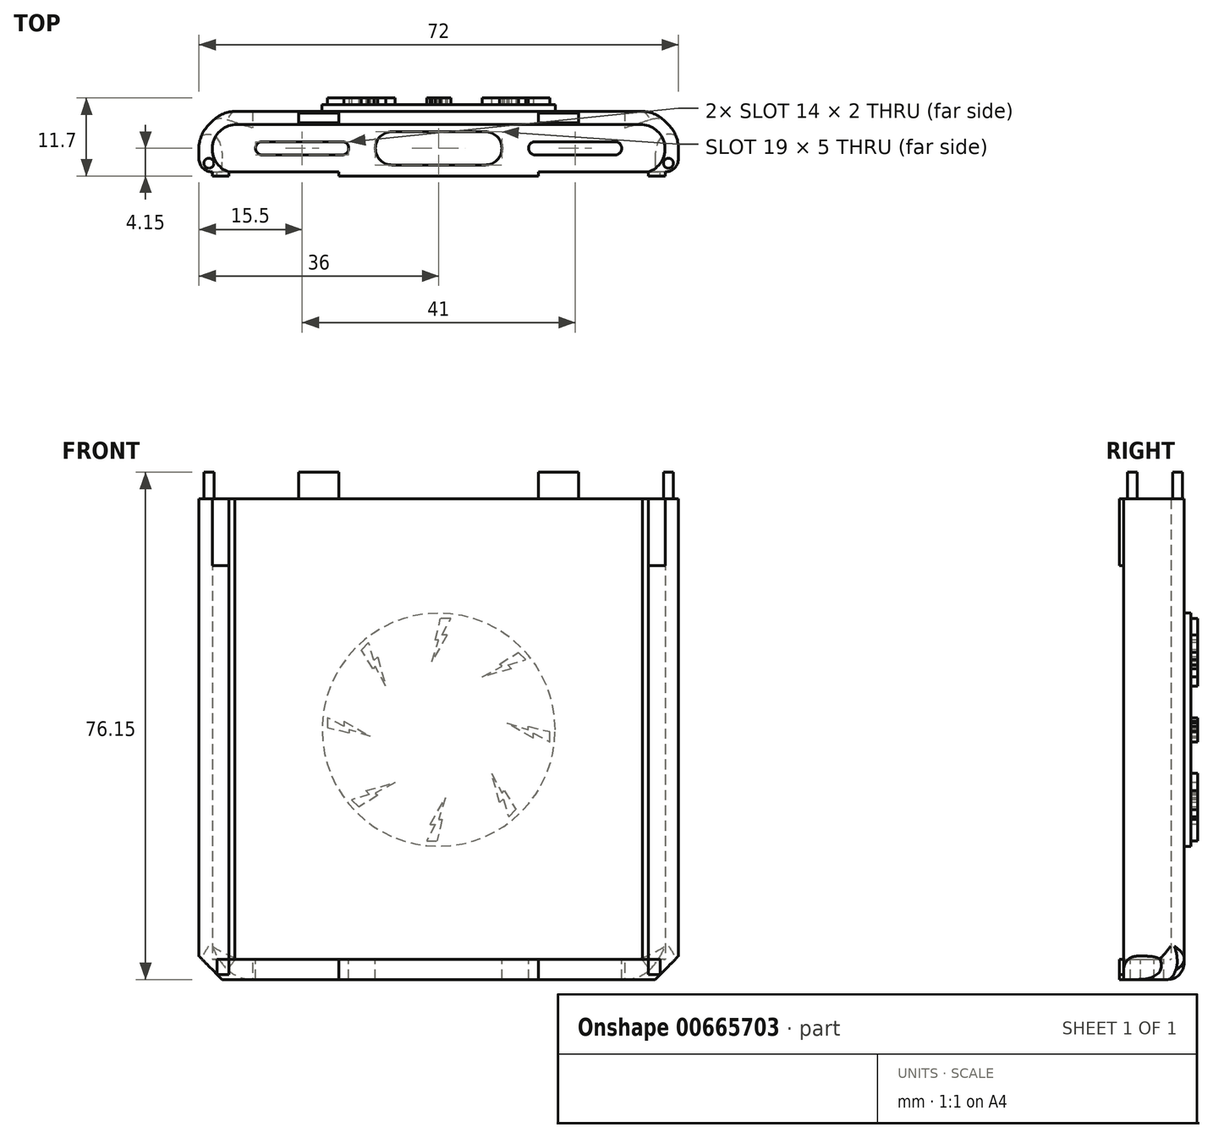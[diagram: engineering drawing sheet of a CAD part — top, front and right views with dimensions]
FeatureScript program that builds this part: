
annotation { "Feature Type Name" : "Feature", "Feature Type Description" : "" }
export const myFeature = defineFeature(function(context is Context, id is Id, definition is map)
    precondition{}
    {
        {
            var Q0;
            Q0=qCreatedBy(makeId("Top.planeOp"),FACE);
            var sketch = newSketch(context, id + "F0", { "sketchPlane" : qUnion([Q0])});
            skLineSegment(sketch, "E0.bottom", {"start": v(-36, 4.55) * mm, "end": v(36, 4.55) * mm});
            skLineSegment(sketch, "E0.top", {"start": v(-36, -4.55) * mm, "end": v(36, -4.55) * mm});
            skLineSegment(sketch, "E0.left", {"start": v(-36, 4.55) * mm, "end": v(-36, -4.55) * mm});
            skLineSegment(sketch, "E0.right", {"start": v(36, 4.55) * mm, "end": v(36, -4.55) * mm});
            skPoint(sketch, "E0.middle", {"position": v(0, 0) * mm});
            skLineSegment(sketch, "E1.bottom", {"start": v(34, -4.55) * mm, "end": v(-34, -4.55) * mm});
            skLineSegment(sketch, "E1.top", {"start": v(34, 2.55) * mm, "end": v(-34, 2.55) * mm});
            skLineSegment(sketch, "E1.left", {"start": v(34, -4.55) * mm, "end": v(34, 2.55) * mm});
            skLineSegment(sketch, "E1.right", {"start": v(-34, -4.55) * mm, "end": v(-34, 2.55) * mm});
            skArc(sketch, "E2", {"start": v(-30.6, 2.55) * mm, "mid": v(-33.97, -0.63) * mm, "end": v(-31.5, -4.55) * mm});
            skArc(sketch, "E3", {"start": v(31.5, -4.55) * mm, "mid": v(33.97, -0.63) * mm, "end": v(30.6, 2.55) * mm});
            skSolve(sketch);
        }
        {
            var Q0;
            Q0=makeQuery(id+"F0.imprint","IMPRINT",FACE,{"disambiguationData":[TD([[makeQuery(id+"F0.imprint","IMPRINT",EDGE,{"derivedFrom":sQuery(id+"F0.wireOp",EDGE,"E0.bottom")}),-1.0]])]});
            var Q1;
            {var subQ0=sQuery(id+"F0.wireOp",EDGE,"E3");var subQ1=sQuery(id+"F0.wireOp",EDGE,"E1.top");var subQ2=makeQuery(id+"F0.imprint","INTERSECT",VERTEX,{"derivedFrom":[subQ1,subQ0]});Q1=makeQuery(id+"F0.imprint","IMPRINT",FACE,{"disambiguationData":[TD([[makeQuery(id+"F0.imprint","IMPRINT",EDGE,{"disambiguationData":[TD([[subQ2,1.0]])],"derivedFrom":subQ1}),1.0]])]});}
            var Q2;
            {var subQ0=sQuery(id+"F0.wireOp",EDGE,"E3");var subQ1=sQuery(id+"F0.wireOp",EDGE,"E0.top");var subQ2=makeQuery(id+"F0.imprint","INTERSECT",VERTEX,{"derivedFrom":[subQ1,subQ0]});Q2=makeQuery(id+"F0.imprint","IMPRINT",FACE,{"disambiguationData":[TD([[makeQuery(id+"F0.imprint","IMPRINT",EDGE,{"disambiguationData":[TD([[subQ2,-1.0]])],"derivedFrom":subQ1}),1.0]])]});}
            var Q3;
            {var subQ0=sQuery(id+"F0.wireOp",EDGE,"E2");var subQ1=sQuery(id+"F0.wireOp",EDGE,"E1.top");var subQ2=makeQuery(id+"F0.imprint","INTERSECT",VERTEX,{"derivedFrom":[subQ1,subQ0]});Q3=makeQuery(id+"F0.imprint","IMPRINT",FACE,{"disambiguationData":[TD([[makeQuery(id+"F0.imprint","IMPRINT",EDGE,{"disambiguationData":[TD([[subQ2,-1.0]])],"derivedFrom":subQ1}),1.0]])]});}
            var Q4;
            {var subQ0=sQuery(id+"F0.wireOp",EDGE,"E2");var subQ1=sQuery(id+"F0.wireOp",EDGE,"E0.top");var subQ2=makeQuery(id+"F0.imprint","INTERSECT",VERTEX,{"derivedFrom":[subQ1,subQ0]});Q4=makeQuery(id+"F0.imprint","IMPRINT",FACE,{"disambiguationData":[TD([[makeQuery(id+"F0.imprint","IMPRINT",EDGE,{"disambiguationData":[TD([[subQ2,1.0]])],"derivedFrom":subQ1}),1.0]])]});}
            extrude(context, id + "F1", {"entities" : qUnion([Q0, Q1, Q2, Q3, Q4]), "depth" : 69.15 * mm, "offsetDistance" : 25 * mm});
        }
        {
            var Q0;
            Q0=makeQuery(id+"F1.opExtrude","CAP_FACE",FACE,{"disambiguationData":[OSD([sQuery(id+"F0.wireOp",EDGE,"E0.bottom"),sQuery(id+"F0.wireOp",EDGE,"E0.top"),sQuery(id+"F0.wireOp",EDGE,"E0.left"),sQuery(id+"F0.wireOp",EDGE,"E0.right"),sQuery(id+"F0.wireOp",EDGE,"E1.top"),sQuery(id+"F0.wireOp",EDGE,"E2"),sQuery(id+"F0.wireOp",EDGE,"E3")])],"isStart":true});
            var sketch = newSketch(context, id + "F2", { "sketchPlane" : qUnion([Q0])});
            skLineSegment(sketch, "E4.bottom", {"start": v(36, 4.55) * mm, "end": v(-36, 4.55) * mm});
            skLineSegment(sketch, "E4.top", {"start": v(36, -4.55) * mm, "end": v(-36, -4.55) * mm});
            skLineSegment(sketch, "E4.left", {"start": v(36, 4.55) * mm, "end": v(36, -4.55) * mm});
            skLineSegment(sketch, "E4.right", {"start": v(-36, 4.55) * mm, "end": v(-36, -4.55) * mm});
            skPoint(sketch, "E4.middle", {"position": v(0, 0) * mm});
            skArc(sketch, "E5", {"start": v(7, -1.5) * mm, "mid": v(9.5, 1) * mm, "end": v(7, 3.5) * mm});
            skArc(sketch, "E6", {"start": v(-7, 3.5) * mm, "mid": v(-9.5, 1) * mm, "end": v(-7, -1.5) * mm});
            skLineSegment(sketch, "E7", {"start": v(-7, 3.5) * mm, "end": v(7, 3.5) * mm});
            skLineSegment(sketch, "E8", {"start": v(-7, -1.5) * mm, "end": v(7, -1.5) * mm});
            skArc(sketch, "E9", {"start": v(-14.5, 0) * mm, "mid": v(-13.5, 1) * mm, "end": v(-14.5, 2) * mm});
            skArc(sketch, "E10", {"start": v(-26.5, 2) * mm, "mid": v(-27.5, 1) * mm, "end": v(-26.5, 0) * mm});
            skLineSegment(sketch, "E11", {"start": v(-26.5, 2) * mm, "end": v(-14.5, 2) * mm});
            skLineSegment(sketch, "E12", {"start": v(-26.5, 0) * mm, "end": v(-14.5, 0) * mm});
            skArc(sketch, "E13", {"start": v(14.5, 2) * mm, "mid": v(13.5, 1) * mm, "end": v(14.5, 0) * mm});
            skArc(sketch, "E14", {"start": v(26.5, 0) * mm, "mid": v(27.5, 1) * mm, "end": v(26.5, 2) * mm});
            skLineSegment(sketch, "E15", {"start": v(14.5, 2) * mm, "end": v(26.5, 2) * mm});
            skLineSegment(sketch, "E16", {"start": v(14.5, 0) * mm, "end": v(26.5, 0) * mm});
            skSolve(sketch);
        }
        {
            var Q0;
            Q0=makeQuery(id+"F2.imprint","IMPRINT",FACE,{"disambiguationData":[TD([[makeQuery(id+"F2.imprint","IMPRINT",EDGE,{"derivedFrom":sQuery(id+"F2.wireOp",EDGE,"E5")}),-1.0]])]});
            var Q1;
            Q1=makeQuery(id+"F2.imprint","IMPRINT",FACE,{"disambiguationData":[TD([[makeQuery(id+"F2.imprint","IMPRINT",EDGE,{"derivedFrom":sQuery(id+"F2.wireOp",EDGE,"E4.top")}),1.0]])]});
            extrude(context, id + "F3", {"entities" : qUnion([Q0, Q1]), "operationType" : NewBodyOperationType.ADD, "depth" : 3 * mm, "offsetDistance" : 25 * mm});
        }
        {
            var Q0;
            Q0=makeQuery(id+"F1.opExtrude","CAP_FACE",FACE,{"disambiguationData":[OSD([sQuery(id+"F0.wireOp",EDGE,"E0.bottom"),sQuery(id+"F0.wireOp",EDGE,"E0.top"),sQuery(id+"F0.wireOp",EDGE,"E0.left"),sQuery(id+"F0.wireOp",EDGE,"E0.right"),sQuery(id+"F0.wireOp",EDGE,"E1.top"),sQuery(id+"F0.wireOp",EDGE,"E2"),sQuery(id+"F0.wireOp",EDGE,"E3")])],"isStart":false});
            var sketch = newSketch(context, id + "F4", { "sketchPlane" : qUnion([Q0])});
            skLineSegment(sketch, "E17.bottom", {"start": v(-21, 4.3) * mm, "end": v(-15, 4.3) * mm});
            skLineSegment(sketch, "E17.top", {"start": v(-21, 2.8) * mm, "end": v(-15, 2.8) * mm});
            skLineSegment(sketch, "E17.left", {"start": v(-21, 4.3) * mm, "end": v(-21, 2.8) * mm});
            skLineSegment(sketch, "E17.right", {"start": v(-15, 4.3) * mm, "end": v(-15, 2.8) * mm});
            skPoint(sketch, "E17.middle", {"position": v(-18, 3.55) * mm});
            skLineSegment(sketch, "E18.bottom", {"start": v(15, 4.3) * mm, "end": v(21, 4.3) * mm});
            skLineSegment(sketch, "E18.top", {"start": v(15, 2.8) * mm, "end": v(21, 2.8) * mm});
            skLineSegment(sketch, "E18.left", {"start": v(15, 4.3) * mm, "end": v(15, 2.8) * mm});
            skLineSegment(sketch, "E18.right", {"start": v(21, 4.3) * mm, "end": v(21, 2.8) * mm});
            skPoint(sketch, "E18.middle", {"position": v(18, 3.55) * mm});
            skCircle(sketch, "E19", {"center": v(-34.5, -3.25) * mm, "radius": 0.75 * mm});
            skCircle(sketch, "E20", {"center": v(34.5, -3.25) * mm, "radius": 0.75 * mm});
            skSolve(sketch);
        }
        {
            var Q0;
            Q0 = qSketchRegion(id + "F4", true);
            extrude(context, id + "F5", {"entities" : qUnion([Q0]), "operationType" : NewBodyOperationType.ADD, "depth" : 4 * mm, "offsetDistance" : 25 * mm});
        }
        {
            var Q0;
            Q0=makeQuery(id+"F3.boolean.opBoolean","MERGE",EDGE,{"derivedFrom":[makeQuery(id+"F1.opExtrude","SWEPT_EDGE",EDGE,{"disambiguationData":[OSD([sQuery(id+"F0.wireOp",EDGE,"E0.bottom"),sQuery(id+"F0.wireOp",EDGE,"E0.left")])]}),makeQuery(id+"F3.opExtrude","SWEPT_EDGE",EDGE,{"disambiguationData":[OSD([sQuery(id+"F2.wireOp",EDGE,"E4.top"),sQuery(id+"F2.wireOp",EDGE,"E4.right")])]})]});
            var Q1;
            Q1=makeQuery(id+"F3.boolean.opBoolean","MERGE",EDGE,{"derivedFrom":[makeQuery(id+"F1.opExtrude","SWEPT_EDGE",EDGE,{"disambiguationData":[OSD([sQuery(id+"F0.wireOp",EDGE,"E0.bottom"),sQuery(id+"F0.wireOp",EDGE,"E0.right")])]}),makeQuery(id+"F3.opExtrude","SWEPT_EDGE",EDGE,{"disambiguationData":[OSD([sQuery(id+"F2.wireOp",EDGE,"E4.top"),sQuery(id+"F2.wireOp",EDGE,"E4.left")])]})]});
            chamfer(context, id + "F6", {"entities" : qUnion([Q0, Q1]), "width" : 3.5 * mm, "tangentPropagation" : true});
        }
        {
            var Q0;
            Q0=makeQuery(id+"F3.opExtrude","CAP_EDGE",EDGE,{"disambiguationData":[OSD([sQuery(id+"F2.wireOp",EDGE,"E4.top")])],"isStart":false});
            fillet(context, id + "F7", {"entities" : qUnion([Q0]), "radius" : 2.5 * mm, "tangentPropagation" : true, "allowEdgeOverflow" : false});
        }
        {
            var Q0;
            Q0=makeQuery(id+"F3.opExtrude","CAP_EDGE",EDGE,{"disambiguationData":[OSD([sQuery(id+"F2.wireOp",EDGE,"E4.left")])],"isStart":false});
            var Q1;
            Q1=makeQuery(id+"F3.opExtrude","CAP_EDGE",EDGE,{"disambiguationData":[OSD([sQuery(id+"F2.wireOp",EDGE,"E4.right")])],"isStart":false});
            chamfer(context, id + "F8", {"entities" : qUnion([Q0, Q1]), "width" : 3.5 * mm, "tangentPropagation" : true});
        }
        {
            var Q0;
            Q0=makeQuery(id+"F3.boolean.opBoolean","MERGE",EDGE,{"derivedFrom":[makeQuery(id+"F1.opExtrude","SWEPT_EDGE",EDGE,{"disambiguationData":[OSD([sQuery(id+"F0.wireOp",EDGE,"E0.top"),sQuery(id+"F0.wireOp",EDGE,"E0.right")])]}),makeQuery(id+"F3.opExtrude","SWEPT_EDGE",EDGE,{"disambiguationData":[OSD([sQuery(id+"F2.wireOp",EDGE,"E4.bottom"),sQuery(id+"F2.wireOp",EDGE,"E4.left")])]})]});
            var Q1;
            Q1=makeQuery(id+"F3.boolean.opBoolean","MERGE",EDGE,{"derivedFrom":[makeQuery(id+"F1.opExtrude","SWEPT_EDGE",EDGE,{"disambiguationData":[OSD([sQuery(id+"F0.wireOp",EDGE,"E0.top"),sQuery(id+"F0.wireOp",EDGE,"E0.left")])]}),makeQuery(id+"F3.opExtrude","SWEPT_EDGE",EDGE,{"disambiguationData":[OSD([sQuery(id+"F2.wireOp",EDGE,"E4.bottom"),sQuery(id+"F2.wireOp",EDGE,"E4.right")])]})]});
            fillet(context, id + "F9", {"entities" : qUnion([Q0, Q1]), "radius" : 2 * mm, "tangentPropagation" : true, "allowEdgeOverflow" : false});
        }
        {
            var Q0;
            {var subQ0=sQuery(id+"F2.wireOp",EDGE,"E4.top");Q0=makeQuery(id+"F7.opFillet","BLEND_EDGE",EDGE,{"blendedFrom":[makeQuery(id+"F3.opExtrude","CAP_EDGE",EDGE,{"disambiguationData":[OSD([subQ0])],"isStart":false}),makeQuery(id+"F6.opChamfer","BLEND_FACE",FACE,{"disambiguationData":[OSD([sQuery(id+"F0.wireOp",EDGE,"E0.bottom"),sQuery(id+"F0.wireOp",EDGE,"E0.left"),subQ0,sQuery(id+"F2.wireOp",EDGE,"E4.right")])]})],"blendedInto":[makeQuery(id+"F6.opChamfer","BLEND_FACE",FACE,{"disambiguationData":[OSD([sQuery(id+"F0.wireOp",EDGE,"E0.bottom"),sQuery(id+"F0.wireOp",EDGE,"E0.left"),subQ0,sQuery(id+"F2.wireOp",EDGE,"E4.right")])]})]});}
            var Q1;
            {var subQ0=sQuery(id+"F2.wireOp",EDGE,"E4.top");Q1=makeQuery(id+"F7.opFillet","BLEND_EDGE",EDGE,{"blendedFrom":[makeQuery(id+"F3.opExtrude","CAP_EDGE",EDGE,{"disambiguationData":[OSD([subQ0])],"isStart":false}),makeQuery(id+"F6.opChamfer","BLEND_FACE",FACE,{"disambiguationData":[OSD([sQuery(id+"F0.wireOp",EDGE,"E0.bottom"),sQuery(id+"F0.wireOp",EDGE,"E0.right"),subQ0,sQuery(id+"F2.wireOp",EDGE,"E4.left")])]})],"blendedInto":[makeQuery(id+"F6.opChamfer","BLEND_FACE",FACE,{"disambiguationData":[OSD([sQuery(id+"F0.wireOp",EDGE,"E0.bottom"),sQuery(id+"F0.wireOp",EDGE,"E0.right"),subQ0,sQuery(id+"F2.wireOp",EDGE,"E4.left")])]})]});}
            fillet(context, id + "F10", {"entities" : qUnion([Q0, Q1]), "radius" : 5 * mm, "tangentPropagation" : true, "allowEdgeOverflow" : false});
        }
        {
            var Q0;
            {var subQ0=sQuery(id+"F2.wireOp",EDGE,"E4.left");var subQ1=sQuery(id+"F0.wireOp",EDGE,"E0.right");Q0=makeQuery(id+"F6.opChamfer","BLEND_EDGE",EDGE,{"blendedFrom":[makeQuery(id+"F3.boolean.opBoolean","MERGE",EDGE,{"derivedFrom":[makeQuery(id+"F1.opExtrude","SWEPT_EDGE",EDGE,{"disambiguationData":[OSD([sQuery(id+"F0.wireOp",EDGE,"E0.bottom"),subQ1])]}),makeQuery(id+"F3.opExtrude","SWEPT_EDGE",EDGE,{"disambiguationData":[OSD([sQuery(id+"F2.wireOp",EDGE,"E4.top"),subQ0])]})]}),makeQuery(id+"F3.boolean.opBoolean","MERGE",FACE,{"derivedFrom":[makeQuery(id+"F1.opExtrude","SWEPT_FACE",FACE,{"disambiguationData":[OSD([subQ1])]}),makeQuery(id+"F3.opExtrude","SWEPT_FACE",FACE,{"disambiguationData":[OSD([subQ0])]})]})],"blendedInto":[makeQuery(id+"F3.boolean.opBoolean","MERGE",FACE,{"derivedFrom":[makeQuery(id+"F1.opExtrude","SWEPT_FACE",FACE,{"disambiguationData":[OSD([subQ1])]}),makeQuery(id+"F3.opExtrude","SWEPT_FACE",FACE,{"disambiguationData":[OSD([subQ0])]})]})]});}
            var Q1;
            {var subQ0=sQuery(id+"F2.wireOp",EDGE,"E4.right");var subQ1=sQuery(id+"F0.wireOp",EDGE,"E0.left");Q1=makeQuery(id+"F6.opChamfer","BLEND_EDGE",EDGE,{"blendedFrom":[makeQuery(id+"F3.boolean.opBoolean","MERGE",EDGE,{"derivedFrom":[makeQuery(id+"F1.opExtrude","SWEPT_EDGE",EDGE,{"disambiguationData":[OSD([sQuery(id+"F0.wireOp",EDGE,"E0.bottom"),subQ1])]}),makeQuery(id+"F3.opExtrude","SWEPT_EDGE",EDGE,{"disambiguationData":[OSD([sQuery(id+"F2.wireOp",EDGE,"E4.top"),subQ0])]})]}),makeQuery(id+"F3.boolean.opBoolean","MERGE",FACE,{"derivedFrom":[makeQuery(id+"F1.opExtrude","SWEPT_FACE",FACE,{"disambiguationData":[OSD([subQ1])]}),makeQuery(id+"F3.opExtrude","SWEPT_FACE",FACE,{"disambiguationData":[OSD([subQ0])]})]})],"blendedInto":[makeQuery(id+"F3.boolean.opBoolean","MERGE",FACE,{"derivedFrom":[makeQuery(id+"F1.opExtrude","SWEPT_FACE",FACE,{"disambiguationData":[OSD([subQ1])]}),makeQuery(id+"F3.opExtrude","SWEPT_FACE",FACE,{"disambiguationData":[OSD([subQ0])]})]})]});}
            fillet(context, id + "F11", {"entities" : qUnion([Q0, Q1]), "radius" : 5 * mm, "tangentPropagation" : true, "allowEdgeOverflow" : false});
        }
        {
            var Q0;
            Q0=makeQuery(id+"F3.boolean.opBoolean","MERGE",FACE,{"derivedFrom":[makeQuery(id+"F1.opExtrude","SWEPT_FACE",FACE,{"disambiguationData":[OSD([sQuery(id+"F0.wireOp",EDGE,"E0.bottom")])]}),makeQuery(id+"F3.opExtrude","SWEPT_FACE",FACE,{"disambiguationData":[OSD([sQuery(id+"F2.wireOp",EDGE,"E4.top")])]})]});
            var sketch = newSketch(context, id + "F12", { "sketchPlane" : qUnion([Q0])});
            skCircle(sketch, "E21", {"center": v(0, 34.5) * mm, "radius": 17.5 * mm});
            skLineSegment(sketch, "E22", {"start": v(-1.25, 48.72) * mm, "end": v(1, 44.72) * mm});
            skLineSegment(sketch, "E23", {"start": v(-1.25, 48.72) * mm, "end": v(-0.5, 48.72) * mm});
            skLineSegment(sketch, "E24", {"start": v(-0.5, 48.72) * mm, "end": v(-1.8, 51.18) * mm});
            skLineSegment(sketch, "E25", {"start": v(1, 44.72) * mm, "end": v(0, 47.95) * mm});
            skLineSegment(sketch, "E26", {"start": v(0, 47.95) * mm, "end": v(0.5, 47.95) * mm});
            skLineSegment(sketch, "E27", {"start": v(0.5, 47.95) * mm, "end": v(-0.26, 51.18) * mm});
            skLineSegment(sketch, "E28", {"start": v(-1.8, 51.18) * mm, "end": v(-0.26, 51.18) * mm});
            skLineSegment(sketch, "E29.1.0", {"start": v(-9.16, 44.37) * mm, "end": v(-11.98, 46.11) * mm});
            skLineSegment(sketch, "E29.1.1", {"start": v(-13.08, 45.02) * mm, "end": v(-11.98, 46.11) * mm});
            skLineSegment(sketch, "E29.1.2", {"start": v(-10.4, 44.2) * mm, "end": v(-13.08, 45.02) * mm});
            skLineSegment(sketch, "E29.1.3", {"start": v(-10.94, 43.67) * mm, "end": v(-10.4, 44.2) * mm});
            skLineSegment(sketch, "E29.1.4", {"start": v(-10.94, 43.67) * mm, "end": v(-6.52, 42.43) * mm});
            skLineSegment(sketch, "E29.1.5", {"start": v(-6.52, 42.43) * mm, "end": v(-9.51, 44.01) * mm});
            skLineSegment(sketch, "E29.1.6", {"start": v(-9.51, 44.01) * mm, "end": v(-9.16, 44.37) * mm});
            skLineSegment(sketch, "E29.2.0", {"start": v(-13.45, 35) * mm, "end": v(-16.68, 34.24) * mm});
            skLineSegment(sketch, "E29.2.1", {"start": v(-16.68, 32.7) * mm, "end": v(-16.68, 34.24) * mm});
            skLineSegment(sketch, "E29.2.2", {"start": v(-14.22, 34) * mm, "end": v(-16.68, 32.7) * mm});
            skLineSegment(sketch, "E29.2.3", {"start": v(-14.22, 33.25) * mm, "end": v(-14.22, 34) * mm});
            skLineSegment(sketch, "E29.2.4", {"start": v(-14.22, 33.25) * mm, "end": v(-10.22, 35.5) * mm});
            skLineSegment(sketch, "E29.2.5", {"start": v(-10.22, 35.5) * mm, "end": v(-13.45, 34.5) * mm});
            skLineSegment(sketch, "E29.2.6", {"start": v(-13.45, 34.5) * mm, "end": v(-13.45, 35) * mm});
            skLineSegment(sketch, "E29.3.0", {"start": v(-9.87, 25.34) * mm, "end": v(-11.61, 22.52) * mm});
            skLineSegment(sketch, "E29.3.1", {"start": v(-10.52, 21.42) * mm, "end": v(-11.61, 22.52) * mm});
            skLineSegment(sketch, "E29.3.2", {"start": v(-9.7, 24.1) * mm, "end": v(-10.52, 21.42) * mm});
            skLineSegment(sketch, "E29.3.3", {"start": v(-9.17, 23.56) * mm, "end": v(-9.7, 24.1) * mm});
            skLineSegment(sketch, "E29.3.4", {"start": v(-9.17, 23.56) * mm, "end": v(-7.93, 27.98) * mm});
            skLineSegment(sketch, "E29.3.5", {"start": v(-7.93, 27.98) * mm, "end": v(-9.51, 24.99) * mm});
            skLineSegment(sketch, "E29.3.6", {"start": v(-9.51, 24.99) * mm, "end": v(-9.87, 25.34) * mm});
            skLineSegment(sketch, "E29.4.0", {"start": v(-0.5, 21.05) * mm, "end": v(0.26, 17.82) * mm});
            skLineSegment(sketch, "E29.4.1", {"start": v(1.8, 17.82) * mm, "end": v(0.26, 17.82) * mm});
            skLineSegment(sketch, "E29.4.2", {"start": v(0.5, 20.28) * mm, "end": v(1.8, 17.82) * mm});
            skLineSegment(sketch, "E29.4.3", {"start": v(1.25, 20.28) * mm, "end": v(0.5, 20.28) * mm});
            skLineSegment(sketch, "E29.4.4", {"start": v(1.25, 20.28) * mm, "end": v(-1, 24.28) * mm});
            skLineSegment(sketch, "E29.4.5", {"start": v(-1, 24.28) * mm, "end": v(0, 21.05) * mm});
            skLineSegment(sketch, "E29.4.6", {"start": v(0, 21.05) * mm, "end": v(-0.5, 21.05) * mm});
            skLineSegment(sketch, "E29.5.0", {"start": v(9.16, 24.63) * mm, "end": v(11.98, 22.89) * mm});
            skLineSegment(sketch, "E29.5.1", {"start": v(13.08, 23.98) * mm, "end": v(11.98, 22.89) * mm});
            skLineSegment(sketch, "E29.5.2", {"start": v(10.4, 24.8) * mm, "end": v(13.08, 23.98) * mm});
            skLineSegment(sketch, "E29.5.3", {"start": v(10.94, 25.33) * mm, "end": v(10.4, 24.8) * mm});
            skLineSegment(sketch, "E29.5.4", {"start": v(10.94, 25.33) * mm, "end": v(6.52, 26.57) * mm});
            skLineSegment(sketch, "E29.5.5", {"start": v(6.52, 26.57) * mm, "end": v(9.51, 24.99) * mm});
            skLineSegment(sketch, "E29.5.6", {"start": v(9.51, 24.99) * mm, "end": v(9.16, 24.63) * mm});
            skLineSegment(sketch, "E29.6.0", {"start": v(13.45, 34) * mm, "end": v(16.68, 34.76) * mm});
            skLineSegment(sketch, "E29.6.1", {"start": v(16.68, 36.3) * mm, "end": v(16.68, 34.76) * mm});
            skLineSegment(sketch, "E29.6.2", {"start": v(14.22, 35) * mm, "end": v(16.68, 36.3) * mm});
            skLineSegment(sketch, "E29.6.3", {"start": v(14.22, 35.75) * mm, "end": v(14.22, 35) * mm});
            skLineSegment(sketch, "E29.6.4", {"start": v(14.22, 35.75) * mm, "end": v(10.22, 33.5) * mm});
            skLineSegment(sketch, "E29.6.5", {"start": v(10.22, 33.5) * mm, "end": v(13.45, 34.5) * mm});
            skLineSegment(sketch, "E29.6.6", {"start": v(13.45, 34.5) * mm, "end": v(13.45, 34) * mm});
            skLineSegment(sketch, "E29.7.0", {"start": v(9.87, 43.66) * mm, "end": v(11.61, 46.48) * mm});
            skLineSegment(sketch, "E29.7.1", {"start": v(10.52, 47.58) * mm, "end": v(11.61, 46.48) * mm});
            skLineSegment(sketch, "E29.7.2", {"start": v(9.7, 44.9) * mm, "end": v(10.52, 47.58) * mm});
            skLineSegment(sketch, "E29.7.3", {"start": v(9.17, 45.44) * mm, "end": v(9.7, 44.9) * mm});
            skLineSegment(sketch, "E29.7.4", {"start": v(9.17, 45.44) * mm, "end": v(7.93, 41.02) * mm});
            skLineSegment(sketch, "E29.7.5", {"start": v(7.93, 41.02) * mm, "end": v(9.51, 44.01) * mm});
            skLineSegment(sketch, "E29.7.6", {"start": v(9.51, 44.01) * mm, "end": v(9.87, 43.66) * mm});
            skSolve(sketch);
        }
        {
            var Q0;
            Q0=makeQuery(id+"F12.imprint","IMPRINT",FACE,{"disambiguationData":[TD([[makeQuery(id+"F12.imprint","IMPRINT",EDGE,{"derivedFrom":sQuery(id+"F12.wireOp",EDGE,"E29.2.0")}),1.0]])]});
            var Q1;
            Q1=makeQuery(id+"F12.imprint","IMPRINT",FACE,{"disambiguationData":[TD([[makeQuery(id+"F12.imprint","IMPRINT",EDGE,{"derivedFrom":sQuery(id+"F12.wireOp",EDGE,"E29.1.0")}),1.0]])]});
            var Q2;
            Q2=makeQuery(id+"F12.imprint","IMPRINT",FACE,{"disambiguationData":[TD([[makeQuery(id+"F12.imprint","IMPRINT",EDGE,{"derivedFrom":sQuery(id+"F12.wireOp",EDGE,"E22")}),1.0]])]});
            var Q3;
            Q3=makeQuery(id+"F12.imprint","IMPRINT",FACE,{"disambiguationData":[TD([[makeQuery(id+"F12.imprint","IMPRINT",EDGE,{"derivedFrom":sQuery(id+"F12.wireOp",EDGE,"E29.7.0")}),1.0]])]});
            var Q4;
            Q4=makeQuery(id+"F12.imprint","IMPRINT",FACE,{"disambiguationData":[TD([[makeQuery(id+"F12.imprint","IMPRINT",EDGE,{"derivedFrom":sQuery(id+"F12.wireOp",EDGE,"E29.6.0")}),1.0]])]});
            var Q5;
            Q5=makeQuery(id+"F12.imprint","IMPRINT",FACE,{"disambiguationData":[TD([[makeQuery(id+"F12.imprint","IMPRINT",EDGE,{"derivedFrom":sQuery(id+"F12.wireOp",EDGE,"E29.5.0")}),1.0]])]});
            var Q6;
            Q6=makeQuery(id+"F12.imprint","IMPRINT",FACE,{"disambiguationData":[TD([[makeQuery(id+"F12.imprint","IMPRINT",EDGE,{"derivedFrom":sQuery(id+"F12.wireOp",EDGE,"E29.4.0")}),1.0]])]});
            var Q7;
            Q7=makeQuery(id+"F12.imprint","IMPRINT",FACE,{"disambiguationData":[TD([[makeQuery(id+"F12.imprint","IMPRINT",EDGE,{"derivedFrom":sQuery(id+"F12.wireOp",EDGE,"E29.3.0")}),1.0]])]});
            extrude(context, id + "F13", {"entities" : qUnion([Q0, Q1, Q2, Q3, Q4, Q5, Q6, Q7]), "operationType" : NewBodyOperationType.ADD, "depth" : 2 * mm, "offsetDistance" : 25 * mm});
        }
        {
            var Q0;
            Q0 = qSketchRegion(id + "F12", true);
            extrude(context, id + "F14", {"entities" : qUnion([Q0]), "operationType" : NewBodyOperationType.ADD, "depth" : 1 * mm, "offsetDistance" : 25 * mm});
        }
        {
            var Q0;
            {var subQ0=sQuery(id+"F0.wireOp",EDGE,"E0.top");Q0=makeQuery(id+"F3.boolean.opBoolean","MERGE",FACE,{"derivedFrom":[makeQuery(id+"F1.opExtrude","SWEPT_FACE",FACE,{"disambiguationData":[OSD([subQ0]),TDD([makeQuery(id+"F0.imprint","IMPRINT",EDGE,{"disambiguationData":[TD([[makeQuery(id+"F0.imprint","INTERSECT",VERTEX,{"derivedFrom":[subQ0,sQuery(id+"F0.wireOp",EDGE,"E3")]}),-1.0]])],"derivedFrom":subQ0}),makeQuery(id+"F0.imprint","IMPRINT",EDGE,{"disambiguationData":[TD([[makeQuery(id+"F0.imprint","INTERSECT",VERTEX,{"derivedFrom":[subQ0,sQuery(id+"F0.wireOp",EDGE,"E0.right")]}),1.0]])],"derivedFrom":subQ0})])]}),makeQuery(id+"F1.opExtrude","SWEPT_FACE",FACE,{"disambiguationData":[OSD([subQ0]),TDD([makeQuery(id+"F0.imprint","IMPRINT",EDGE,{"disambiguationData":[TD([[makeQuery(id+"F0.imprint","INTERSECT",VERTEX,{"derivedFrom":[subQ0,sQuery(id+"F0.wireOp",EDGE,"E2")]}),1.0]])],"derivedFrom":subQ0}),makeQuery(id+"F0.imprint","IMPRINT",EDGE,{"disambiguationData":[TD([[makeQuery(id+"F0.imprint","INTERSECT",VERTEX,{"derivedFrom":[subQ0,sQuery(id+"F0.wireOp",EDGE,"E0.left")]}),-1.0]])],"derivedFrom":subQ0})])]}),makeQuery(id+"F3.opExtrude","SWEPT_FACE",FACE,{"disambiguationData":[OSD([sQuery(id+"F2.wireOp",EDGE,"E4.bottom")])]})]});}
            var sketch = newSketch(context, id + "F15", { "sketchPlane" : qUnion([Q0])});
            skLineSegment(sketch, "E30.bottom", {"start": v(-31.5, 0) * mm, "end": v(-33.25, 0) * mm});
            skLineSegment(sketch, "E30.top", {"start": v(-31.5, -2.25) * mm, "end": v(-33.25, -2.25) * mm});
            skLineSegment(sketch, "E30.left", {"start": v(-31.5, 0) * mm, "end": v(-31.5, -2.25) * mm});
            skLineSegment(sketch, "E30.right", {"start": v(-33.25, 0) * mm, "end": v(-33.25, -2.25) * mm});
            skLineSegment(sketch, "E31.bottom", {"start": v(31.5, 0) * mm, "end": v(33.25, 0) * mm});
            skLineSegment(sketch, "E31.top", {"start": v(31.5, -2.25) * mm, "end": v(33.25, -2.25) * mm});
            skLineSegment(sketch, "E31.left", {"start": v(31.5, 0) * mm, "end": v(31.5, -2.25) * mm});
            skLineSegment(sketch, "E31.right", {"start": v(33.25, 0) * mm, "end": v(33.25, -2.25) * mm});
            skLineSegment(sketch, "E32.bottom", {"start": v(-15, 0) * mm, "end": v(15, 0) * mm});
            skLineSegment(sketch, "E32.top", {"start": v(-15, -3) * mm, "end": v(15, -3) * mm});
            skLineSegment(sketch, "E32.left", {"start": v(-15, 0) * mm, "end": v(-15, -3) * mm});
            skLineSegment(sketch, "E32.right", {"start": v(15, 0) * mm, "end": v(15, -3) * mm});
            skLineSegment(sketch, "E33.bottom", {"start": v(34, 69.15) * mm, "end": v(31.5, 69.15) * mm});
            skLineSegment(sketch, "E33.top", {"start": v(34, 59.15) * mm, "end": v(31.5, 59.15) * mm});
            skLineSegment(sketch, "E33.left", {"start": v(34, 69.15) * mm, "end": v(34, 59.15) * mm});
            skLineSegment(sketch, "E33.right", {"start": v(31.5, 69.15) * mm, "end": v(31.5, 59.15) * mm});
            skLineSegment(sketch, "E34.bottom", {"start": v(-34, 69.15) * mm, "end": v(-31.5, 69.15) * mm});
            skLineSegment(sketch, "E34.top", {"start": v(-34, 59.15) * mm, "end": v(-31.5, 59.15) * mm});
            skLineSegment(sketch, "E34.left", {"start": v(-34, 69.15) * mm, "end": v(-34, 59.15) * mm});
            skLineSegment(sketch, "E34.right", {"start": v(-31.5, 69.15) * mm, "end": v(-31.5, 59.15) * mm});
            skSolve(sketch);
        }
        {
            var Q0;
            Q0 = qSketchRegion(id + "F15", true);
            extrude(context, id + "F16", {"entities" : qUnion([Q0]), "operationType" : NewBodyOperationType.ADD, "depth" : 0.6 * mm, "offsetDistance" : 25 * mm});
        }
    });
